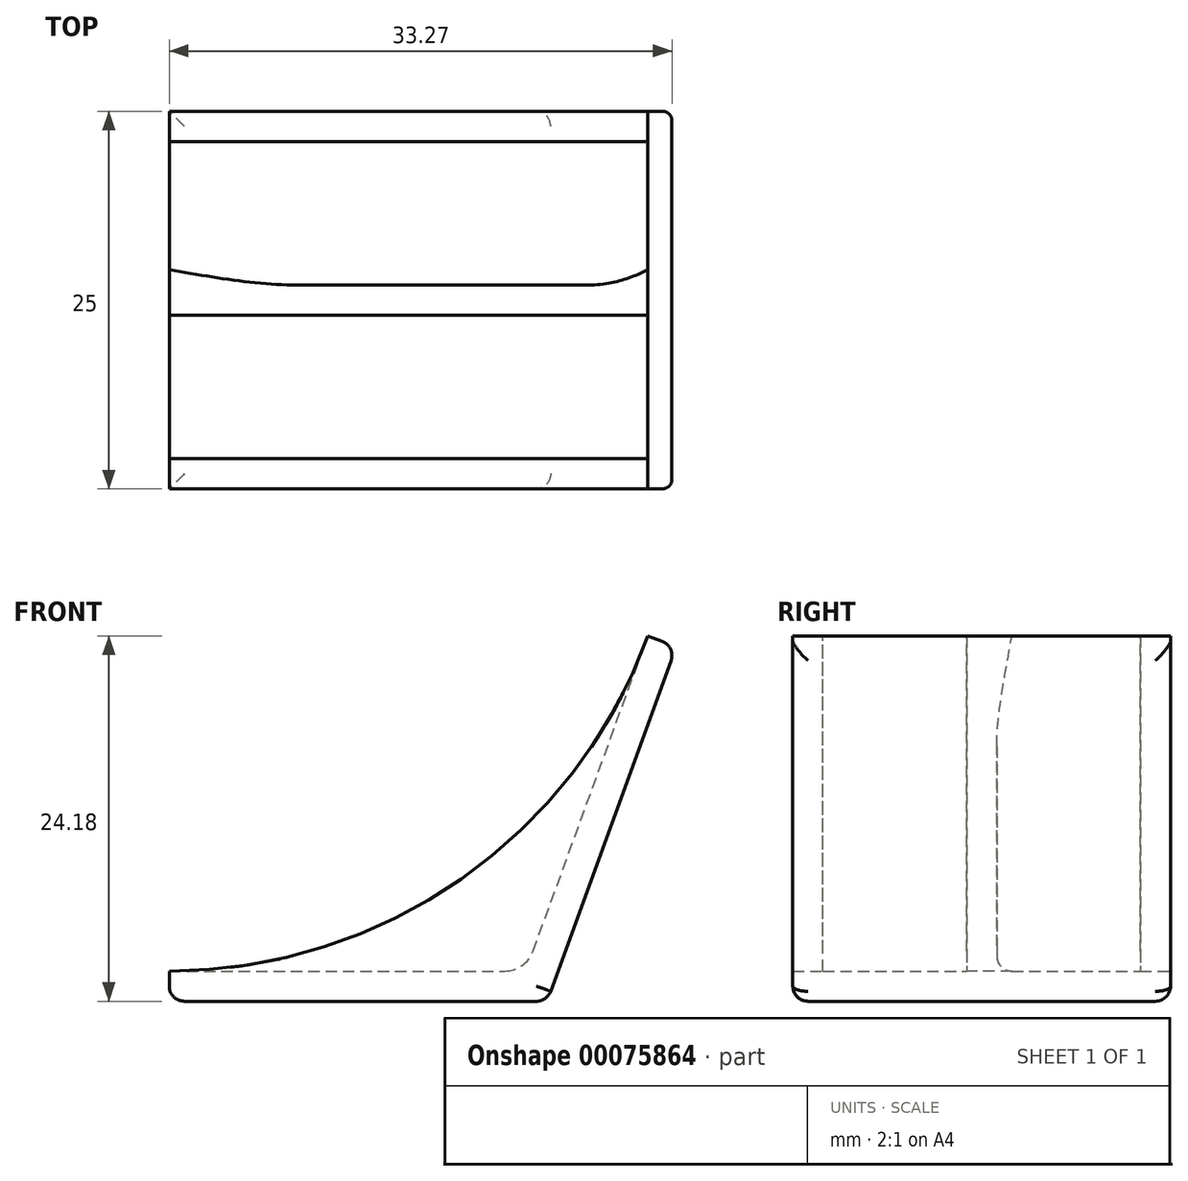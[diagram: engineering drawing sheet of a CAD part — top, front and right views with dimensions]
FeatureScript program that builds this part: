
annotation { "Feature Type Name" : "Feature", "Feature Type Description" : "" }
export const myFeature = defineFeature(function(context is Context, id is Id, definition is map)
    precondition{}
    {
        {
            var Q0;
            Q0=qCreatedBy(makeId("Front.planeOp"),FACE);
            var sketch = newSketch(context, id + "F0", { "sketchPlane" : qUnion([Q0])});
            skLineSegment(sketch, "E0", {"start": v(0, 0) * mm, "end": v(-25, 0) * mm});
            skLineSegment(sketch, "E1", {"start": v(-25, 0) * mm, "end": v(-25, 2) * mm});
            skLineSegment(sketch, "E2", {"start": v(6.67, 24.18) * mm, "end": v(8.55, 23.5) * mm});
            skLineSegment(sketch, "E3", {"start": v(8.55, 23.5) * mm, "end": v(0, 0) * mm});
            skLineSegment(sketch, "E4", {"start": v(-25, 2) * mm, "end": v(-1.4, 2) * mm});
            skLineSegment(sketch, "E5", {"start": v(-1.4, 2) * mm, "end": v(6.67, 24.18) * mm});
            skSolve(sketch);
        }
        {
            var Q0;
            Q0=qSketchRegion(id+"F0",true);
            extrude(context, id + "F1", {"entities" : qUnion([Q0]), "depth" : 25 * mm});
        }
        {
            var Q0;
            Q0=makeQuery(id+"F1.opExtrude","CAP_FACE",FACE,{"disambiguationData":[OSD([sQuery(id+"F0.wireOp",EDGE,"E0"),sQuery(id+"F0.wireOp",EDGE,"E1"),sQuery(id+"F0.wireOp",EDGE,"E2"),sQuery(id+"F0.wireOp",EDGE,"E3"),sQuery(id+"F0.wireOp",EDGE,"E4"),sQuery(id+"F0.wireOp",EDGE,"E5")])],"isStart":true});
            var sketch = newSketch(context, id + "F2", { "sketchPlane" : qUnion([Q0])});
            skLineSegment(sketch, "E6.0", {"start": v(1.4, 2) * mm, "end": v(-6.67, 24.18) * mm});
            skLineSegment(sketch, "E7.0", {"start": v(25, 2) * mm, "end": v(1.4, 2) * mm});
            skArc(sketch, "E8", {"start": v(-6.67, 24.18) * mm, "mid": v(5.67, 8.1) * mm, "end": v(25, 2) * mm});
            skSolve(sketch);
        }
        {
            var Q0;
            Q0=qSketchRegion(id+"F2",true);
            extrude(context, id + "F3", {"entities" : qUnion([Q0]), "operationType" : NewBodyOperationType.ADD, "oppositeDirection" : true, "depth" : 2 * mm});
        }
        {
            var Q0;
            Q0=makeQuery(id+"F1.opExtrude","CAP_FACE",FACE,{"disambiguationData":[OSD([sQuery(id+"F0.wireOp",EDGE,"E0"),sQuery(id+"F0.wireOp",EDGE,"E1"),sQuery(id+"F0.wireOp",EDGE,"E2"),sQuery(id+"F0.wireOp",EDGE,"E3"),sQuery(id+"F0.wireOp",EDGE,"E4"),sQuery(id+"F0.wireOp",EDGE,"E5")])],"isStart":false});
            var sketch = newSketch(context, id + "F4", { "sketchPlane" : qUnion([Q0])});
            skLineSegment(sketch, "E9.0", {"start": v(-1.4, 2) * mm, "end": v(6.67, 24.18) * mm});
            skLineSegment(sketch, "E10.0", {"start": v(-25, 2) * mm, "end": v(-1.4, 2) * mm});
            skArc(sketch, "E11", {"start": v(-25, 2) * mm, "mid": v(-5.67, 8.1) * mm, "end": v(6.67, 24.18) * mm});
            skSolve(sketch);
        }
        {
            var Q0;
            Q0=qSketchRegion(id+"F4",true);
            extrude(context, id + "F5", {"entities" : qUnion([Q0]), "operationType" : NewBodyOperationType.ADD, "oppositeDirection" : true, "depth" : 2 * mm});
        }
        {
            var Q0;
            Q0=makeQuery(id+"F3.boolean.opBoolean","MERGE",FACE,{"derivedFrom":[makeQuery(id+"F1.opExtrude","CAP_FACE",FACE,{"disambiguationData":[OSD([sQuery(id+"F0.wireOp",EDGE,"E0"),sQuery(id+"F0.wireOp",EDGE,"E1"),sQuery(id+"F0.wireOp",EDGE,"E2"),sQuery(id+"F0.wireOp",EDGE,"E3"),sQuery(id+"F0.wireOp",EDGE,"E4"),sQuery(id+"F0.wireOp",EDGE,"E5")])],"isStart":true}),makeQuery(id+"F3.opExtrude","CAP_FACE",FACE,{"disambiguationData":[OSD([sQuery(id+"F2.wireOp",EDGE,"E6.0"),sQuery(id+"F2.wireOp",EDGE,"E7.0"),sQuery(id+"F2.wireOp",EDGE,"E8")])],"isStart":true})]});
            var Q1;
            Q1=makeQuery(id+"F5.boolean.opBoolean","MERGE",FACE,{"derivedFrom":[makeQuery(id+"F1.opExtrude","CAP_FACE",FACE,{"disambiguationData":[OSD([sQuery(id+"F0.wireOp",EDGE,"E0"),sQuery(id+"F0.wireOp",EDGE,"E1"),sQuery(id+"F0.wireOp",EDGE,"E2"),sQuery(id+"F0.wireOp",EDGE,"E3"),sQuery(id+"F0.wireOp",EDGE,"E4"),sQuery(id+"F0.wireOp",EDGE,"E5")])],"isStart":false}),makeQuery(id+"F5.opExtrude","CAP_FACE",FACE,{"disambiguationData":[OSD([sQuery(id+"F4.wireOp",EDGE,"E9.0"),sQuery(id+"F4.wireOp",EDGE,"E10.0"),sQuery(id+"F4.wireOp",EDGE,"E11")])],"isStart":true})]});
            cPlane(context, id + "F6", {"entities" : qUnion([Q0, Q1]), "cplaneType" : CPlaneType.MID_PLANE, "offset" : 152.4 * mm, "width" : 152.4 * mm, "height" : 152.4 * mm});
        }
        {
            var Q0;
            Q0=qCreatedBy(id+"F6.planeOp",FACE);
            var sketch = newSketch(context, id + "F7", { "sketchPlane" : qUnion([Q0])});
            skArc(sketch, "E12.0.0", {"start": v(-6.67, 24.18) * mm, "mid": v(5.67, 8.1) * mm, "end": v(25, 2) * mm});
            skLineSegment(sketch, "E12.0.1", {"start": v(25, 2) * mm, "end": v(1.4, 2) * mm});
            skLineSegment(sketch, "E12.0.2", {"start": v(1.4, 2) * mm, "end": v(-6.67, 24.18) * mm});
            skLineSegment(sketch, "E12.1", {"start": v(1.4, 2) * mm, "end": v(-6.67, 24.18) * mm});
            skSolve(sketch);
        }
        {
            var Q0;
            Q0=qSketchRegion(id+"F7",true);
            extrude(context, id + "F8", {"entities" : qUnion([Q0]), "operationType" : NewBodyOperationType.ADD, "depth" : 1 * mm, "hasSecondDirection" : true, "secondDirectionOppositeDirection" : true, "secondDirectionDepth" : 1 * mm});
        }
        {
            var Q0;
            Q0=makeQuery(id+"F1.opExtrude","SWEPT_FACE",FACE,{"disambiguationData":[OSD([sQuery(id+"F0.wireOp",EDGE,"E3")])]});
            fillet(context, id + "F9", {"entities" : qUnion([Q0]), "radius" : 1 * mm, "tangentPropagation" : true, "allowEdgeOverflow" : false});
        }
        {
            var Q0;
            Q0=makeQuery(id+"F1.opExtrude","SWEPT_FACE",FACE,{"disambiguationData":[OSD([sQuery(id+"F0.wireOp",EDGE,"E0")])]});
            fillet(context, id + "F10", {"entities" : qUnion([Q0]), "radius" : 1 * mm, "tangentPropagation" : true, "allowEdgeOverflow" : false});
        }
        {
            var Q0;
            {var subQ0=sQuery(id+"F0.wireOp",EDGE,"E4");var subQ1=sQuery(id+"F0.wireOp",EDGE,"E5");Q0=makeQuery(id+"F8.boolean.opBoolean","SPLIT",EDGE,{"disambiguationData":[TD([makeQuery(id+"F3.opExtrude","CAP_FACE",FACE,{"disambiguationData":[OSD([sQuery(id+"F2.wireOp",EDGE,"E6.0"),sQuery(id+"F2.wireOp",EDGE,"E7.0"),sQuery(id+"F2.wireOp",EDGE,"E8")])],"isStart":false})])],"derivedFrom":makeQuery(id+"F1.opExtrude","SWEPT_EDGE",EDGE,{"disambiguationData":[OSD([subQ0,subQ1])]})});}
            var Q1;
            {var subQ0=sQuery(id+"F0.wireOp",EDGE,"E4");var subQ1=sQuery(id+"F0.wireOp",EDGE,"E5");Q1=makeQuery(id+"F8.boolean.opBoolean","SPLIT",EDGE,{"disambiguationData":[TD([makeQuery(id+"F5.opExtrude","CAP_FACE",FACE,{"disambiguationData":[OSD([sQuery(id+"F4.wireOp",EDGE,"E9.0"),sQuery(id+"F4.wireOp",EDGE,"E10.0"),sQuery(id+"F4.wireOp",EDGE,"E11")])],"isStart":false})])],"derivedFrom":makeQuery(id+"F1.opExtrude","SWEPT_EDGE",EDGE,{"disambiguationData":[OSD([subQ0,subQ1])]})});}
            fillet(context, id + "F11", {"entities" : qUnion([Q0, Q1]), "radius" : 2 * mm, "tangentPropagation" : true, "allowEdgeOverflow" : false});
        }
        {
            var Q0;
            Q0=makeQuery(id+"F3.opExtrude","CAP_EDGE",EDGE,{"disambiguationData":[OSD([sQuery(id+"F2.wireOp",EDGE,"E7.0")])],"isStart":false});
            var Q1;
            Q1=makeQuery(id+"F8.opExtrude","CAP_EDGE",EDGE,{"disambiguationData":[OSD([sQuery(id+"F7.wireOp",EDGE,"E12.0.1")])],"isStart":false});
            var Q2;
            Q2=makeQuery(id+"F5.opExtrude","CAP_EDGE",EDGE,{"disambiguationData":[OSD([sQuery(id+"F4.wireOp",EDGE,"E10.0")])],"isStart":false});
            var Q3;
            Q3=makeQuery(id+"F8.opExtrude","CAP_EDGE",EDGE,{"disambiguationData":[OSD([sQuery(id+"F7.wireOp",EDGE,"E12.0.1")])],"isStart":true});
            fillet(context, id + "F12", {"entities" : qUnion([Q0, Q1, Q2, Q3]), "radius" : 1 * mm, "tangentPropagation" : true, "allowEdgeOverflow" : false});
        }
    });
